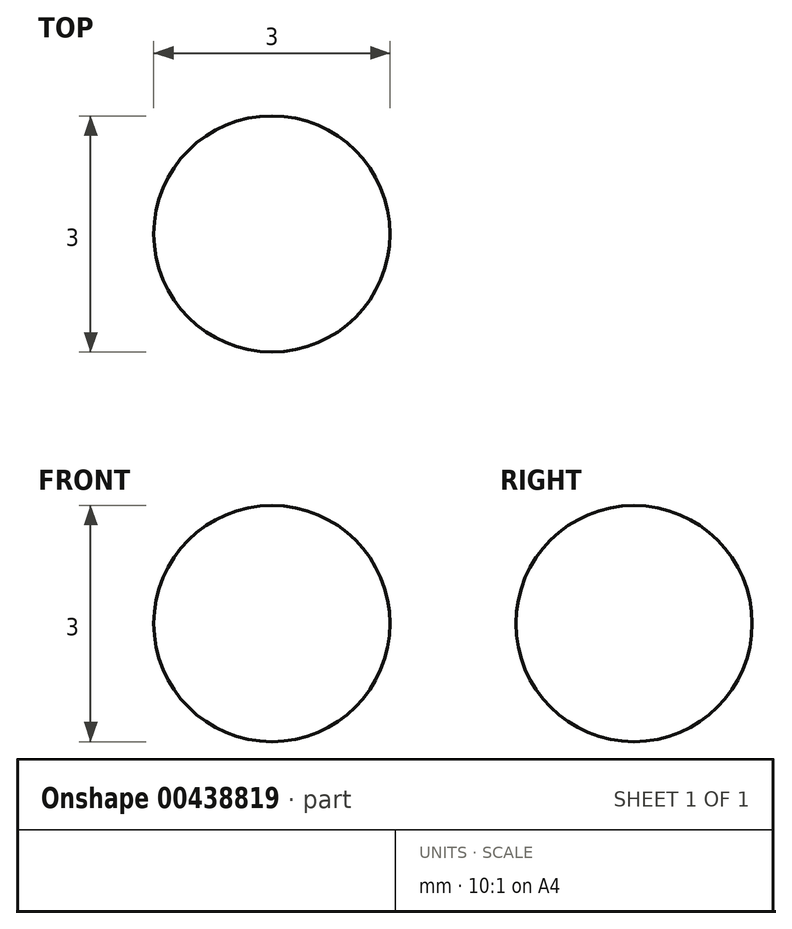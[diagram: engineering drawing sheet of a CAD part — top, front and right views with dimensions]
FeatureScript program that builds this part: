
annotation { "Feature Type Name" : "Feature", "Feature Type Description" : "" }
export const myFeature = defineFeature(function(context is Context, id is Id, definition is map)
    precondition{}
    {
        {
            var Q0;
            Q0=qCreatedBy(makeId("Top.planeOp"),FACE);
            var sketch = newSketch(context, id + "F0", { "sketchPlane" : qUnion([Q0])});
            skArc(sketch, "E0", {"start": v(0, -1.5) * mm, "mid": v(1.5, 0) * mm, "end": v(0, 1.5) * mm});
            skLineSegment(sketch, "E1", {"start": v(0, 0) * mm, "end": v(0, 2.32) * mm, "construction": true});
            skLineSegment(sketch, "E2", {"start": v(0, -1.5) * mm, "end": v(0, 1.5) * mm});
            skSolve(sketch);
        }
        {
            var Q0;
            Q0=makeQuery(id+"F0.imprint","IMPRINT",FACE,{"disambiguationData":[TD([[makeQuery(id+"F0.imprint","IMPRINT",EDGE,{"derivedFrom":sQuery(id+"F0.wireOp",EDGE,"E0")}),1.0]])]});
            var Q1;
            Q1=sQuery(id+"F0.wireOp",EDGE,"E1");
            revolve(context, id + "F1", {"entities" : qUnion([Q0]), "axis" : qUnion([Q1]), "revolveType" : RevolveType.FULL});
        }
    });
